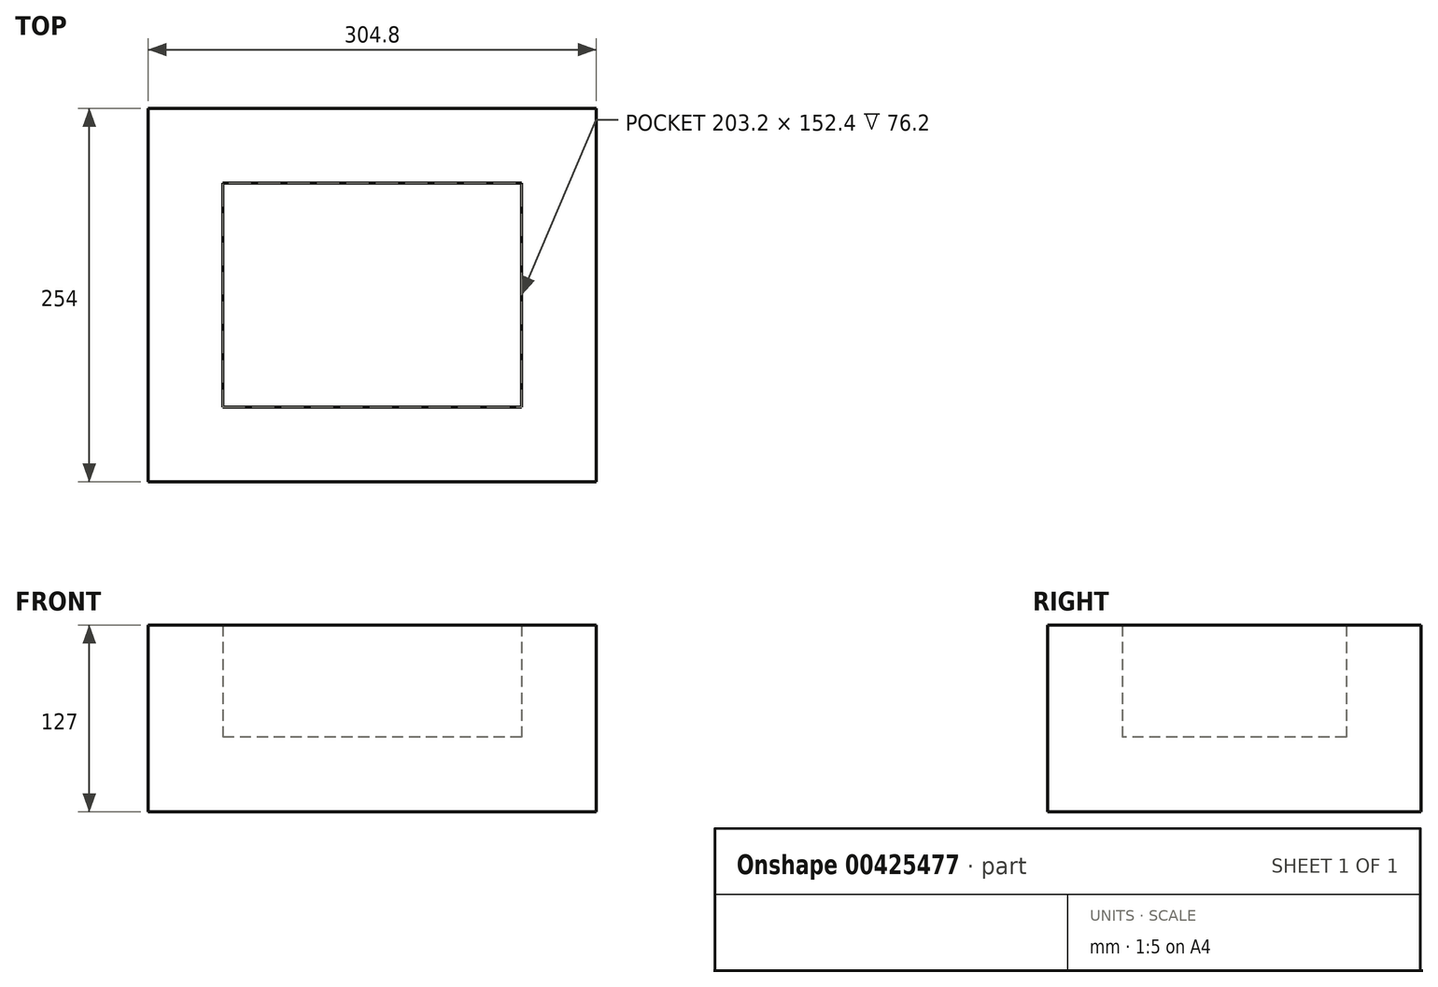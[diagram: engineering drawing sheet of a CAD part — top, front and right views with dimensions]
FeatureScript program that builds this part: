
annotation { "Feature Type Name" : "Feature", "Feature Type Description" : "" }
export const myFeature = defineFeature(function(context is Context, id is Id, definition is map)
    precondition{}
    {
        {
            var Q0;
            Q0=qCreatedBy(makeId("Top.planeOp"),FACE);
            var sketch = newSketch(context, id + "F0", { "sketchPlane" : qUnion([Q0])});
            skLineSegment(sketch, "E0.bottom", {"start": v(152.4, 127) * mm, "end": v(-152.4, 127) * mm});
            skLineSegment(sketch, "E0.top", {"start": v(152.4, -127) * mm, "end": v(-152.4, -127) * mm});
            skLineSegment(sketch, "E0.left", {"start": v(152.4, 127) * mm, "end": v(152.4, -127) * mm});
            skLineSegment(sketch, "E0.right", {"start": v(-152.4, 127) * mm, "end": v(-152.4, -127) * mm});
            skPoint(sketch, "E0.middle", {"position": v(0, 0) * mm});
            skLineSegment(sketch, "E1.top", {"start": v(-152.4, -127) * mm, "end": v(-101.6, -127) * mm});
            skSolve(sketch);
        }
        {
            var Q0;
            Q0=makeQuery(id+"F0.imprint","IMPRINT",FACE,{"disambiguationData":[TD([[makeQuery(id+"F0.imprint","IMPRINT",EDGE,{"derivedFrom":sQuery(id+"F0.wireOp",EDGE,"E0.bottom")}),1.0]])]});
            extrude(context, id + "F1", {"entities" : qUnion([Q0]), "depth" : 127 * mm});
        }
        {
            var Q0;
            Q0=makeQuery(id+"F1.opExtrude","CAP_FACE",FACE,{"disambiguationData":[OSD([sQuery(id+"F0.wireOp",EDGE,"E0.bottom"),sQuery(id+"F0.wireOp",EDGE,"E0.top"),sQuery(id+"F0.wireOp",EDGE,"E0.left"),sQuery(id+"F0.wireOp",EDGE,"E0.right")])],"isStart":false});
            shell(context, id + "F2", {"entities" : qUnion([Q0]), "thickness" : 50.8 * mm});
        }
    });
